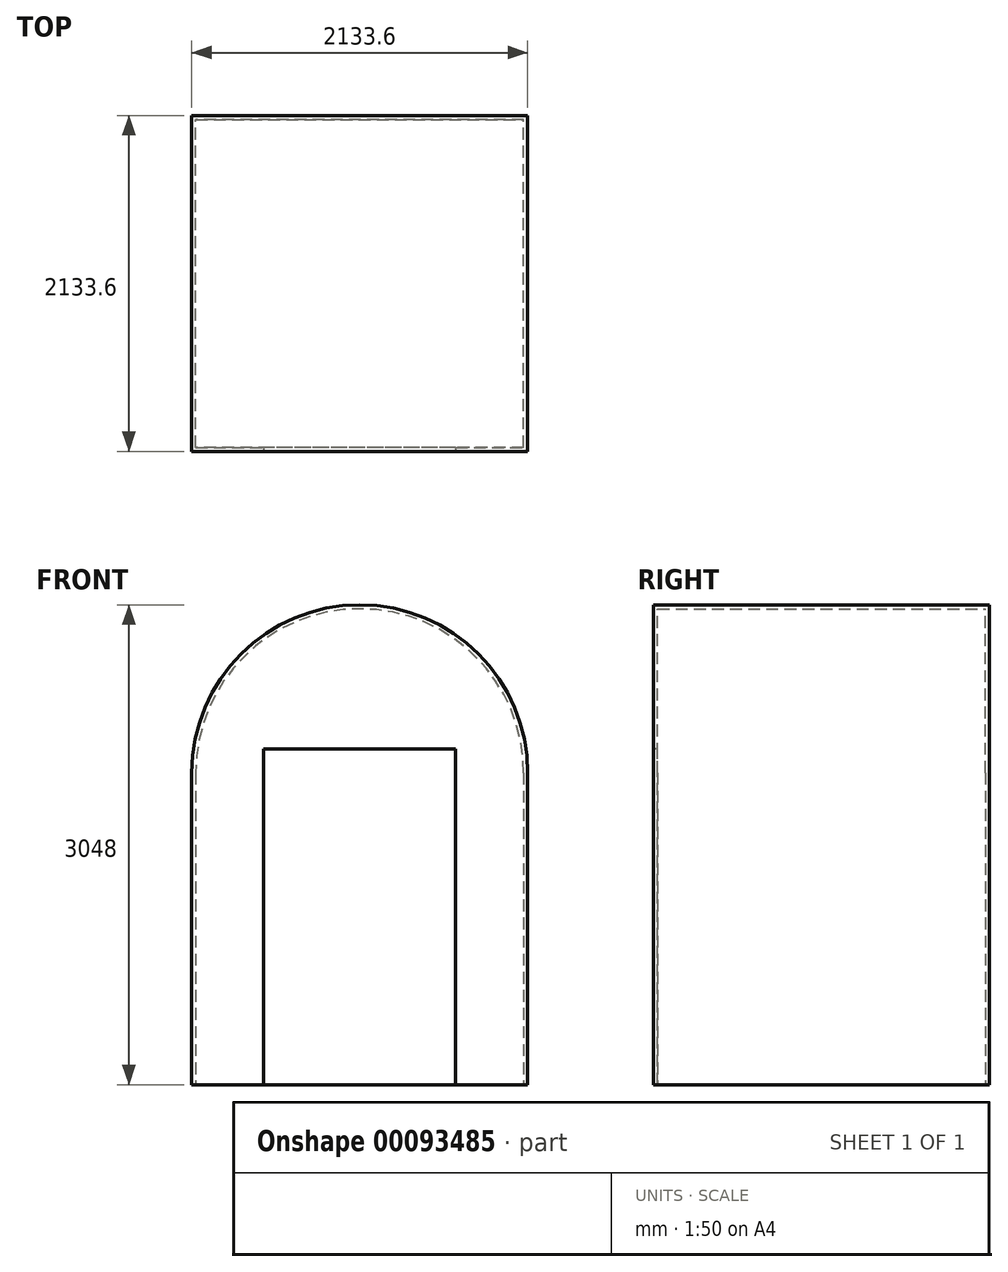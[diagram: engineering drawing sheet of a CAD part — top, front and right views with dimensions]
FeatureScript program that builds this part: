
annotation { "Feature Type Name" : "Feature", "Feature Type Description" : "" }
export const myFeature = defineFeature(function(context is Context, id is Id, definition is map)
    precondition{}
    {
        {
            var Q0;
            Q0=qCreatedBy(makeId("Front.planeOp"),FACE);
            var sketch = newSketch(context, id + "F0", { "sketchPlane" : qUnion([Q0])});
            skLineSegment(sketch, "E0.top", {"start": v(-74.52, -1852.49) * mm, "end": v(2059.08, -1852.49) * mm});
            skLineSegment(sketch, "E0.left", {"start": v(-74.52, 128.71) * mm, "end": v(-74.52, -1852.49) * mm});
            skLineSegment(sketch, "E0.right", {"start": v(2059.08, 128.71) * mm, "end": v(2059.08, -1852.49) * mm});
            skArc(sketch, "E1", {"start": v(2059.08, 128.71) * mm, "mid": v(992.28, 1195.51) * mm, "end": v(-74.52, 128.71) * mm});
            skSolve(sketch);
        }
        {
            var Q0;
            Q0=makeQuery(id+"F0.imprint","IMPRINT",FACE,{"disambiguationData":[TD([[makeQuery(id+"F0.imprint","IMPRINT",EDGE,{"derivedFrom":sQuery(id+"F0.wireOp",EDGE,"E0.top")}),1.0]])]});
            extrude(context, id + "F1", {"entities" : qUnion([Q0]), "endBound" : BoundingType.SYMMETRIC, "depth" : 2133.6 * mm});
        }
        {
            var Q0;
            Q0=makeQuery(id+"F1.opExtrude","CAP_FACE",FACE,{"disambiguationData":[OSD([sQuery(id+"F0.wireOp",EDGE,"E0.top"),sQuery(id+"F0.wireOp",EDGE,"E0.left"),sQuery(id+"F0.wireOp",EDGE,"E0.right"),sQuery(id+"F0.wireOp",EDGE,"E1")])],"isStart":false});
            var sketch = newSketch(context, id + "F2", { "sketchPlane" : qUnion([Q0])});
            skLineSegment(sketch, "E2.bottom", {"start": v(382.68, 281.11) * mm, "end": v(1601.88, 281.11) * mm});
            skLineSegment(sketch, "E2.top", {"start": v(382.68, -1852.49) * mm, "end": v(1601.88, -1852.49) * mm});
            skLineSegment(sketch, "E2.left", {"start": v(382.68, 281.11) * mm, "end": v(382.68, -1852.49) * mm});
            skLineSegment(sketch, "E2.right", {"start": v(1601.88, 281.11) * mm, "end": v(1601.88, -1852.49) * mm});
            skSolve(sketch);
        }
        {
            var Q0;
            Q0 = qSketchRegion(id + "F2", true);
            extrude(context, id + "F3", {"entities" : qUnion([Q0]), "operationType" : NewBodyOperationType.REMOVE, "oppositeDirection" : true, "depth" : 2108.2 * mm});
        }
        {
            var Q0;
            Q0=qCreatedBy(makeId("Front.planeOp"),FACE);
            var sketch = newSketch(context, id + "F4", { "sketchPlane" : qUnion([Q0])});
            skLineSegment(sketch, "E3.top", {"start": v(-49.12, -1852.49) * mm, "end": v(2033.68, -1852.49) * mm});
            skLineSegment(sketch, "E3.left", {"start": v(-49.12, 128.71) * mm, "end": v(-49.12, -1852.49) * mm});
            skLineSegment(sketch, "E3.right", {"start": v(2033.68, 128.71) * mm, "end": v(2033.68, -1852.49) * mm});
            skArc(sketch, "E4", {"start": v(2033.68, 128.71) * mm, "mid": v(992.28, 1170.11) * mm, "end": v(-49.12, 128.71) * mm});
            skSolve(sketch);
        }
        {
            var Q0;
            Q0 = qSketchRegion(id + "F4", true);
            extrude(context, id + "F5", {"entities" : qUnion([Q0]), "operationType" : NewBodyOperationType.REMOVE, "endBound" : BoundingType.SYMMETRIC, "depth" : 2082.8 * mm});
        }
    });
